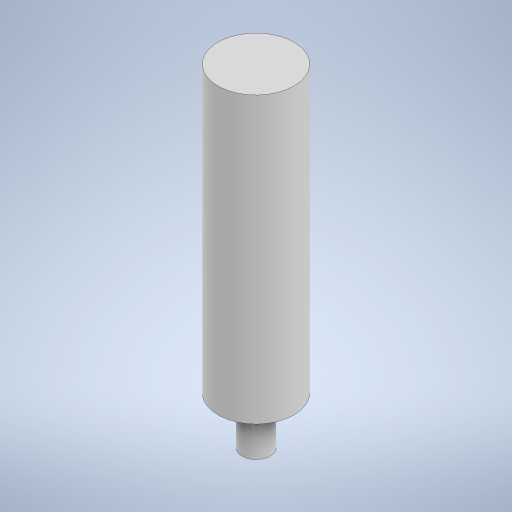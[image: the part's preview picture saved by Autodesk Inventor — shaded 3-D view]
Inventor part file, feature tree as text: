
AUTODESK INVENTOR PART (.ipt)
format: ipt  version: 2024.2 (Build 282272000, 272)  size: 226,304 bytes
history: native  units: mm
features: extrude x2, sketch x2
ambient origin geometry x8: Origin, YZ Plane, XZ Plane, XY Plane, X Axis, Y Axis, Z Axis, Center Point
bodies: Solid1 (feature_tree)
feature tree (4):
  extrude  "Extrusion1"  Depth=5.0mm TaperAngle=0.0deg
  extrude  "Extrusion2"  Depth=30.0mm TaperAngle=0.0deg
  sketch  "Sketch1"  dims[d0=3.0mm d1=5.0mm d2=0.0mm]
  sketch  "Sketch2"  dims[d3=8.0mm d4=30.0mm d5=0.0mm]
